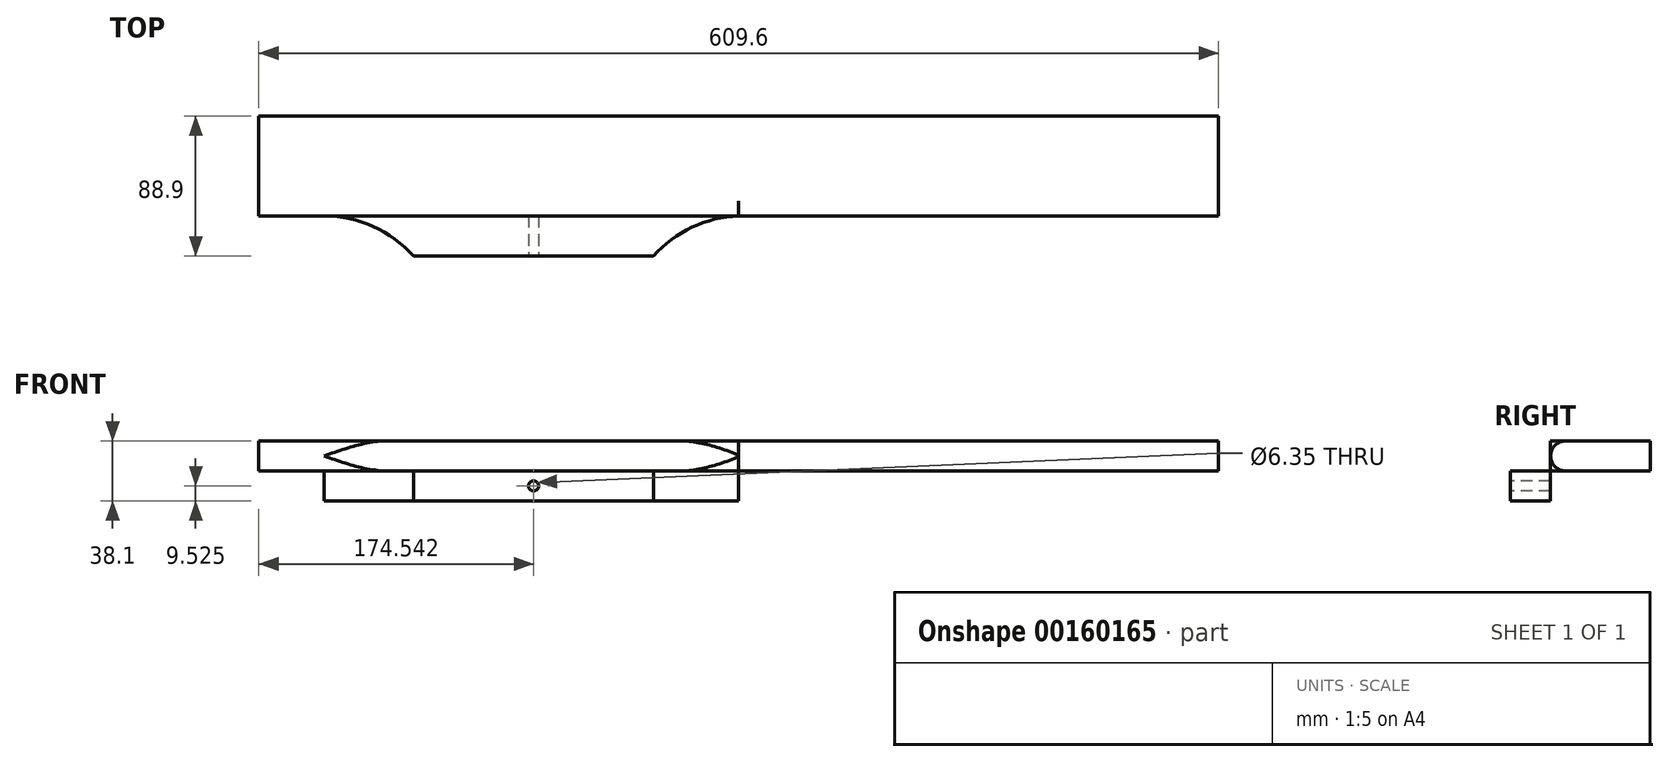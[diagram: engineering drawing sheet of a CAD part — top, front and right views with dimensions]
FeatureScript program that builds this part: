
annotation { "Feature Type Name" : "Feature", "Feature Type Description" : "" }
export const myFeature = defineFeature(function(context is Context, id is Id, definition is map)
    precondition{}
    {
        {
            var Q0;
            Q0=qCreatedBy(makeId("Front.planeOp"),FACE);
            var sketch = newSketch(context, id + "F0", { "sketchPlane" : qUnion([Q0])});
            skLineSegment(sketch, "E0", {"start": v(0, 0) * mm, "end": v(439.85, 0) * mm});
            skLineSegment(sketch, "E1", {"start": v(439.85, 0) * mm, "end": v(439.85, 140.59) * mm, "construction": true});
            skLineSegment(sketch, "E2", {"start": v(439.85, 140.59) * mm, "end": v(413.5, 0) * mm});
            skLineSegment(sketch, "E3", {"start": v(439.85, 140.59) * mm, "end": v(375.23, 140.59) * mm});
            skLineSegment(sketch, "E4", {"start": v(310.46, 79.12) * mm, "end": v(7.02, 37.45) * mm});
            skLineSegment(sketch, "E5", {"start": v(7.02, 37.45) * mm, "end": v(0, 0) * mm});
            skPoint(sketch, "E6.visualSharp", {"position": v(351.86, 84.8) * mm});
            skArc(sketch, "E7", {"start": v(310.46, 79.12) * mm, "mid": v(352.74, 99.43) * mm, "end": v(375.23, 140.59) * mm});
            skSolve(sketch);
        }
        {
            var Q0;
            Q0=qCreatedBy(makeId("Top.planeOp"),FACE);
            var sketch = newSketch(context, id + "F1", { "sketchPlane" : qUnion([Q0])});
            skLineSegment(sketch, "E8.bottom", {"start": v(-609.6, -48.92) * mm, "end": v(0, -48.92) * mm});
            skLineSegment(sketch, "E8.top", {"start": v(-609.6, -112.42) * mm, "end": v(0, -112.42) * mm});
            skLineSegment(sketch, "E8.left", {"start": v(-609.6, -48.92) * mm, "end": v(-609.6, -112.42) * mm});
            skLineSegment(sketch, "E8.right", {"start": v(0, -48.92) * mm, "end": v(0, -112.42) * mm});
            skArc(sketch, "E9", {"start": v(-304.8, -112.42) * mm, "mid": v(-334.42, -119.6) * mm, "end": v(-358.86, -137.82) * mm});
            skLineSegment(sketch, "E10", {"start": v(-358.86, -137.82) * mm, "end": v(-511.26, -137.82) * mm});
            skArc(sketch, "E11", {"start": v(-511.26, -137.82) * mm, "mid": v(-536.95, -119.06) * mm, "end": v(-568.05, -112.42) * mm});
            skSolve(sketch);
        }
        {
            var Q0;
            Q0=makeQuery(id+"F1.imprint","IMPRINT",FACE,{"disambiguationData":[TD([[makeQuery(id+"F1.imprint","IMPRINT",EDGE,{"derivedFrom":sQuery(id+"F1.wireOp",EDGE,"E8.bottom")}),-1.0]])]});
            var Q1;
            {var subQ2=sQuery(id+"F1.wireOp",EDGE,"E9");Q1=makeQuery(id+"F1.imprint","IMPRINT",FACE,{"disambiguationData":[TD([[makeQuery(id+"F1.imprint","IMPRINT",EDGE,{"derivedFrom":subQ2}),-1.0]])]});}
            extrude(context, id + "F2", {"entities" : qUnion([Q0, Q1]), "depth" : 19.05 * mm});
        }
        {
            var Q0;
            Q0=makeQuery(id+"F2.opExtrude","CAP_EDGE",EDGE,{"disambiguationData":[OSD([sQuery(id+"F1.wireOp",EDGE,"E8.top")])],"isStart":false});
            var Q1;
            Q1=makeQuery(id+"F2.opExtrude","CAP_EDGE",EDGE,{"disambiguationData":[OSD([sQuery(id+"F1.wireOp",EDGE,"E8.top")])],"isStart":true});
            fillet(context, id + "F3", {"entities" : qUnion([Q0, Q1]), "radius" : 9.52 * mm, "tangentPropagation" : true, "allowEdgeOverflow" : false});
        }
        {
            var Q0;
            {var subQ2=sQuery(id+"F1.wireOp",EDGE,"E9");Q0=makeQuery(id+"F1.imprint","IMPRINT",FACE,{"disambiguationData":[TD([[makeQuery(id+"F1.imprint","IMPRINT",EDGE,{"derivedFrom":subQ2}),-1.0]])]});}
            extrude(context, id + "F4", {"entities" : qUnion([Q0]), "operationType" : NewBodyOperationType.REMOVE, "endBound" : BoundingType.THROUGH_ALL, "depth" : 25.4 * mm});
        }
        {
            var Q0;
            {var subQ0=sQuery(id+"F1.wireOp",EDGE,"E9");Q0=makeQuery(id+"F1.imprint","IMPRINT",FACE,{"disambiguationData":[TD([[makeQuery(id+"F1.imprint","IMPRINT",EDGE,{"derivedFrom":subQ0}),-1.0]])]});}
            extrude(context, id + "F5", {"entities" : qUnion([Q0]), "oppositeDirection" : true, "depth" : 19.05 * mm});
        }
        {
            var Q0;
            Q0=makeQuery(id+"F5.opExtrude","SWEPT_FACE",FACE,{"disambiguationData":[OSD([sQuery(id+"F1.wireOp",EDGE,"E10")])]});
            var sketch = newSketch(context, id + "F6", { "sketchPlane" : qUnion([Q0])});
            skCircle(sketch, "E12", {"center": v(-435.06, -9.53) * mm, "radius": 3.18 * mm});
            skPoint(sketch, "E12.centerSnap0", {"position": v(-435.06, -19.05) * mm});
            skPoint(sketch, "E12.centerSnap1", {"position": v(-511.26, -9.53) * mm});
            skSolve(sketch);
        }
        {
            var Q0;
            Q0=makeQuery(id+"F6.imprint","IMPRINT",FACE,{"disambiguationData":[TD([[makeQuery(id+"F6.imprint","IMPRINT",EDGE,{"derivedFrom":sQuery(id+"F6.wireOp",EDGE,"E12")}),1.0]])]});
            extrude(context, id + "F7", {"entities" : qUnion([Q0]), "operationType" : NewBodyOperationType.REMOVE, "endBound" : BoundingType.THROUGH_ALL, "oppositeDirection" : true, "depth" : 25.4 * mm});
        }
    });
